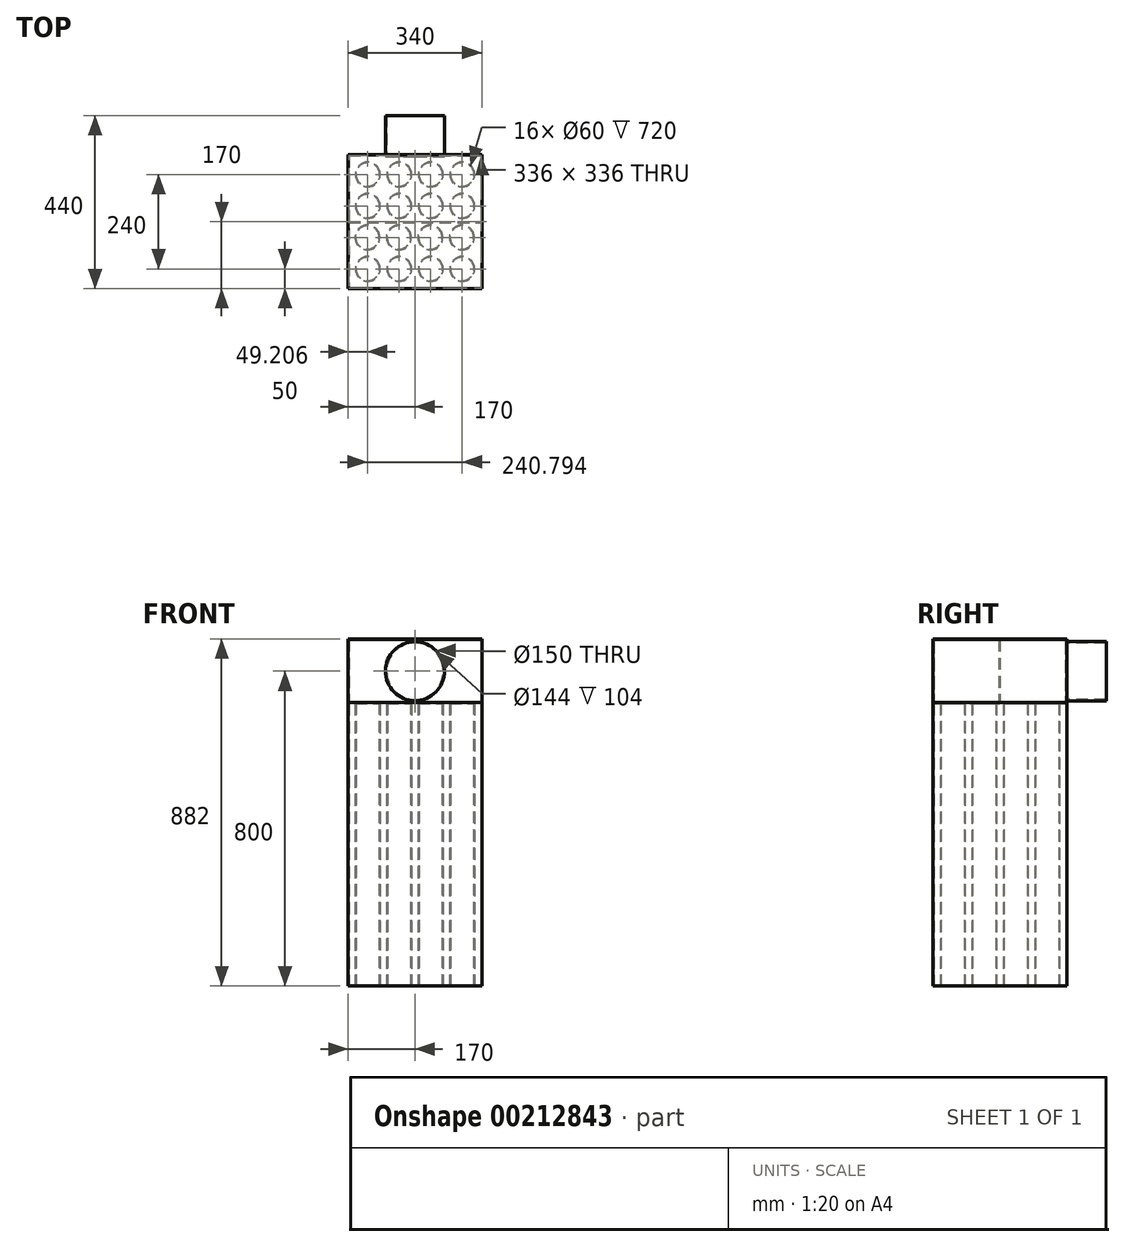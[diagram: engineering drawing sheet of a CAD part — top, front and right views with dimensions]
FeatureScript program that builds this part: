
annotation { "Feature Type Name" : "Feature", "Feature Type Description" : "" }
export const myFeature = defineFeature(function(context is Context, id is Id, definition is map)
    precondition{}
    {
        {
            var Q0;
            Q0=qCreatedBy(makeId("Top.planeOp"),FACE);
            var sketch = newSketch(context, id + "F0", { "sketchPlane" : qUnion([Q0])});
            skLineSegment(sketch, "E0.bottom", {"start": v(-170, 30.7) * mm, "end": v(170, 30.7) * mm});
            skLineSegment(sketch, "E0.top", {"start": v(-170, -309.3) * mm, "end": v(170, -309.3) * mm});
            skLineSegment(sketch, "E0.left", {"start": v(-170, 30.7) * mm, "end": v(-170, -309.3) * mm});
            skLineSegment(sketch, "E0.right", {"start": v(170, 30.7) * mm, "end": v(170, -309.3) * mm});
            skCircle(sketch, "E1", {"center": v(-120, -19.3) * mm, "radius": 30 * mm});
            skLineSegment(sketch, "E2.MirrorCS", {"start": v(-169.6, 306.05) * mm, "end": v(180.4, 306.05) * mm});
            skCircle(sketch, "E3", {"center": v(-40, -19.3) * mm, "radius": 30 * mm});
            skCircle(sketch, "E4", {"center": v(40, -19.3) * mm, "radius": 30 * mm});
            skCircle(sketch, "E5", {"center": v(120, -19.3) * mm, "radius": 30 * mm});
            skLineSegment(sketch, "E6", {"start": v(-170, 10.7) * mm, "end": v(170, 10.7) * mm, "construction": true});
            skLineSegment(sketch, "E7", {"start": v(150, 30.7) * mm, "end": v(150, -309.3) * mm, "construction": true});
            skCircle(sketch, "E8", {"center": v(120, -99.3) * mm, "radius": 30 * mm});
            skLineSegment(sketch, "E9", {"start": v(-170, -69.3) * mm, "end": v(170, -69.3) * mm, "construction": true});
            skLineSegment(sketch, "E10", {"start": v(-172.66, -149.3) * mm, "end": v(167.46, -149.3) * mm, "construction": true});
            skCircle(sketch, "E11", {"center": v(-120.8, -179.3) * mm, "radius": 30 * mm});
            skCircle(sketch, "E12", {"center": v(-40.8, -179.3) * mm, "radius": 30 * mm});
            skCircle(sketch, "E13", {"center": v(39.2, -179.3) * mm, "radius": 30 * mm});
            skCircle(sketch, "E14", {"center": v(119.2, -179.3) * mm, "radius": 30 * mm});
            skLineSegment(sketch, "E15", {"start": v(70, 30.7) * mm, "end": v(70, -309.3) * mm, "construction": true});
            skLineSegment(sketch, "E16", {"start": v(-10, 30.7) * mm, "end": v(-10, -309.3) * mm, "construction": true});
            skLineSegment(sketch, "E17", {"start": v(-90, 30.7) * mm, "end": v(-90, -309.3) * mm, "construction": true});
            skLineSegment(sketch, "E18", {"start": v(-170, -229.3) * mm, "end": v(170, -229.3) * mm, "construction": true});
            skCircle(sketch, "E19", {"center": v(-120, -99.3) * mm, "radius": 30 * mm});
            skCircle(sketch, "E20", {"center": v(-40, -99.3) * mm, "radius": 30 * mm});
            skCircle(sketch, "E21", {"center": v(40, -99.3) * mm, "radius": 30 * mm});
            skCircle(sketch, "E22", {"center": v(-120, -259.3) * mm, "radius": 30 * mm});
            skCircle(sketch, "E23", {"center": v(-40, -259.3) * mm, "radius": 30 * mm});
            skCircle(sketch, "E24", {"center": v(40, -259.3) * mm, "radius": 30 * mm});
            skCircle(sketch, "E25", {"center": v(120, -259.3) * mm, "radius": 30 * mm});
            skSolve(sketch);
        }
        {
            var Q0;
            Q0=makeQuery(id+"F0.imprint","IMPRINT",FACE,{"disambiguationData":[TD([[makeQuery(id+"F0.imprint","IMPRINT",EDGE,{"derivedFrom":sQuery(id+"F0.wireOp",EDGE,"E0.bottom")}),-1.0]])]});
            extrude(context, id + "F1", {"entities" : qUnion([Q0]), "endBound" : BoundingType.SYMMETRIC, "depth" : 720 * mm});
        }
        {
            var Q0;
            Q0=makeQuery(id+"F1.opExtrude","CAP_FACE",FACE,{"disambiguationData":[OSD([sQuery(id+"F0.wireOp",EDGE,"E0.bottom"),sQuery(id+"F0.wireOp",EDGE,"E0.top"),sQuery(id+"F0.wireOp",EDGE,"E0.left"),sQuery(id+"F0.wireOp",EDGE,"E0.right"),sQuery(id+"F0.wireOp",EDGE,"E1"),sQuery(id+"F0.wireOp",EDGE,"E3"),sQuery(id+"F0.wireOp",EDGE,"E4"),sQuery(id+"F0.wireOp",EDGE,"E5"),sQuery(id+"F0.wireOp",EDGE,"E8"),sQuery(id+"F0.wireOp",EDGE,"E11"),sQuery(id+"F0.wireOp",EDGE,"E12"),sQuery(id+"F0.wireOp",EDGE,"E13"),sQuery(id+"F0.wireOp",EDGE,"E14"),sQuery(id+"F0.wireOp",EDGE,"E19"),sQuery(id+"F0.wireOp",EDGE,"E20"),sQuery(id+"F0.wireOp",EDGE,"E21"),sQuery(id+"F0.wireOp",EDGE,"E22"),sQuery(id+"F0.wireOp",EDGE,"E23"),sQuery(id+"F0.wireOp",EDGE,"E24"),sQuery(id+"F0.wireOp",EDGE,"E25")])],"isStart":false});
            var sketch = newSketch(context, id + "F2", { "sketchPlane" : qUnion([Q0])});
            skLineSegment(sketch, "E26.0", {"start": v(-168, 28.7) * mm, "end": v(-168, -307.3) * mm});
            skLineSegment(sketch, "E26.1", {"start": v(-168, 28.7) * mm, "end": v(168, 28.7) * mm});
            skLineSegment(sketch, "E26.2", {"start": v(168, 28.7) * mm, "end": v(168, -307.3) * mm});
            skLineSegment(sketch, "E26.3", {"start": v(-168, -307.3) * mm, "end": v(168, -307.3) * mm});
            skSolve(sketch);
        }
        {
            var Q0;
            Q0=makeQuery(id+"F2.imprint","IMPRINT",FACE,{"disambiguationData":[TD([[makeQuery(id+"F2.imprint","IMPRINT",EDGE,{"derivedFrom":sQuery(id+"F2.wireOp",EDGE,"E26.0")}),-1.0]])]});
            extrude(context, id + "F3", {"entities" : qUnion([Q0]), "depth" : 160 * mm});
        }
        {
            var Q0;
            Q0=makeQuery(id+"F3.opExtrude","SWEPT_FACE",FACE,{"disambiguationData":[OSD([sQuery(id+"F2.wireOp",EDGE,"E26.2")])]});
            var sketch = newSketch(context, id + "F4", { "sketchPlane" : qUnion([Q0])});
            skLineSegment(sketch, "E27.bottom", {"start": v(139.3, 520) * mm, "end": v(141.3, 520) * mm});
            skLineSegment(sketch, "E27.top", {"start": v(139.3, 360) * mm, "end": v(141.3, 360) * mm});
            skLineSegment(sketch, "E27.left", {"start": v(139.3, 520) * mm, "end": v(139.3, 360) * mm});
            skLineSegment(sketch, "E27.right", {"start": v(141.3, 520) * mm, "end": v(141.3, 360) * mm});
            skLineSegment(sketch, "E28", {"start": v(140.3, 520) * mm, "end": v(140.3, 360) * mm, "construction": true});
            skSolve(sketch);
        }
        {
            var Q0;
            Q0=makeQuery(id+"F4.imprint","IMPRINT",FACE,{"disambiguationData":[TD([[makeQuery(id+"F4.imprint","IMPRINT",EDGE,{"derivedFrom":sQuery(id+"F4.wireOp",EDGE,"E27.bottom")}),-1.0]])]});
            extrude(context, id + "F5", {"entities" : qUnion([Q0]), "depth" : 336 * mm});
        }
        {
            var Q0;
            Q0=makeQuery(id+"F3.opExtrude","CAP_FACE",FACE,{"disambiguationData":[OSD([sQuery(id+"F0.wireOp",EDGE,"E0.bottom"),sQuery(id+"F0.wireOp",EDGE,"E0.top"),sQuery(id+"F0.wireOp",EDGE,"E0.left"),sQuery(id+"F0.wireOp",EDGE,"E0.right"),sQuery(id+"F2.wireOp",EDGE,"E26.0"),sQuery(id+"F2.wireOp",EDGE,"E26.1"),sQuery(id+"F2.wireOp",EDGE,"E26.2"),sQuery(id+"F2.wireOp",EDGE,"E26.3")])],"isStart":false});
            var sketch = newSketch(context, id + "F6", { "sketchPlane" : qUnion([Q0])});
            skLineSegment(sketch, "E29.bottom", {"start": v(-170, 30.7) * mm, "end": v(170, 30.7) * mm});
            skLineSegment(sketch, "E29.top", {"start": v(-170, -309.3) * mm, "end": v(170, -309.3) * mm});
            skLineSegment(sketch, "E29.left", {"start": v(-170, 30.7) * mm, "end": v(-170, -309.3) * mm});
            skLineSegment(sketch, "E29.right", {"start": v(170, 30.7) * mm, "end": v(170, -309.3) * mm});
            skSolve(sketch);
        }
        {
            var Q0;
            Q0 = qSketchRegion(id + "F6", true);
            extrude(context, id + "F7", {"entities" : qUnion([Q0]), "depth" : 2 * mm});
        }
        {
            var Q0;
            Q0=makeQuery(id+"F3.opExtrude","SWEPT_FACE",FACE,{"disambiguationData":[OSD([sQuery(id+"F0.wireOp",EDGE,"E0.top")])]});
            var sketch = newSketch(context, id + "F8", { "sketchPlane" : qUnion([Q0])});
            skCircle(sketch, "E30", {"center": v(0, 440) * mm, "radius": 75 * mm});
            skPoint(sketch, "E30.centerSnap0", {"position": v(170, 440) * mm});
            skSolve(sketch);
        }
        {
            var Q0;
            Q0 = qSketchRegion(id + "F8", true);
            extrude(context, id + "F9", {"entities" : qUnion([Q0]), "operationType" : NewBodyOperationType.REMOVE, "endBound" : BoundingType.SYMMETRIC, "depth" : 25 * mm});
        }
        {
            var Q0;
            Q0=makeQuery(id+"F3.opExtrude","SWEPT_FACE",FACE,{"disambiguationData":[OSD([sQuery(id+"F0.wireOp",EDGE,"E0.top")])]});
            var sketch = newSketch(context, id + "F10", { "sketchPlane" : qUnion([Q0])});
            skCircle(sketch, "E31", {"center": v(0, 440) * mm, "radius": 75 * mm});
            skCircle(sketch, "E32.0", {"center": v(0, 440) * mm, "radius": 72 * mm});
            skSolve(sketch);
        }
        {
            var Q0;
            Q0=sQuery(id+"F10.wireOp",EDGE,"E32.0");
            var Q1;
            Q1=sQuery(id+"F10.wireOp",EDGE,"E31");
            extrude(context, id + "F11", {"bodyType" : ToolBodyType.SURFACE, "surfaceEntities" : qUnion([Q0, Q1]), "depth" : 100 * mm, "hasSecondDirection" : true, "secondDirectionOppositeDirection" : true, "secondDirectionDepth" : 6 * mm});
        }
        {
            var Q0;
            Q0=makeQuery(id+"F3.opExtrude","SWEPT_FACE",FACE,{"disambiguationData":[OSD([sQuery(id+"F0.wireOp",EDGE,"E0.bottom")])]});
            var sketch = newSketch(context, id + "F12", { "sketchPlane" : qUnion([Q0])});
            skCircle(sketch, "E33", {"center": v(0, 440) * mm, "radius": 75 * mm});
            skPoint(sketch, "E33.centerSnap0", {"position": v(170, 440) * mm});
            skSolve(sketch);
        }
        {
            var Q0;
            Q0 = qSketchRegion(id + "F12", true);
            extrude(context, id + "F13", {"entities" : qUnion([Q0]), "operationType" : NewBodyOperationType.REMOVE, "oppositeDirection" : true, "depth" : 25 * mm});
        }
        {
            var Q0;
            Q0=makeQuery(id+"F3.opExtrude","SWEPT_FACE",FACE,{"disambiguationData":[OSD([sQuery(id+"F0.wireOp",EDGE,"E0.bottom")])]});
            var sketch = newSketch(context, id + "F14", { "sketchPlane" : qUnion([Q0])});
            skCircle(sketch, "E34", {"center": v(0, 440) * mm, "radius": 75 * mm});
            skCircle(sketch, "E35.0", {"center": v(0, 440) * mm, "radius": 72 * mm});
            skSolve(sketch);
        }
        {
            var Q0;
            Q0 = qSketchRegion(id + "F14", true);
            extrude(context, id + "F15", {"entities" : qUnion([Q0]), "operationType" : NewBodyOperationType.ADD, "depth" : 100 * mm, "hasSecondDirection" : true, "secondDirectionOppositeDirection" : true, "secondDirectionDepth" : 4 * mm});
        }
        {
            var Q0;
            Q0=makeQuery(id+"F1.opExtrude","CAP_FACE",FACE,{"disambiguationData":[OSD([sQuery(id+"F0.wireOp",EDGE,"E0.bottom"),sQuery(id+"F0.wireOp",EDGE,"E0.top"),sQuery(id+"F0.wireOp",EDGE,"E0.left"),sQuery(id+"F0.wireOp",EDGE,"E0.right"),sQuery(id+"F0.wireOp",EDGE,"E1"),sQuery(id+"F0.wireOp",EDGE,"E3"),sQuery(id+"F0.wireOp",EDGE,"E4"),sQuery(id+"F0.wireOp",EDGE,"E5"),sQuery(id+"F0.wireOp",EDGE,"E8"),sQuery(id+"F0.wireOp",EDGE,"E11"),sQuery(id+"F0.wireOp",EDGE,"E12"),sQuery(id+"F0.wireOp",EDGE,"E13"),sQuery(id+"F0.wireOp",EDGE,"E14"),sQuery(id+"F0.wireOp",EDGE,"E19"),sQuery(id+"F0.wireOp",EDGE,"E20"),sQuery(id+"F0.wireOp",EDGE,"E21"),sQuery(id+"F0.wireOp",EDGE,"E22"),sQuery(id+"F0.wireOp",EDGE,"E23"),sQuery(id+"F0.wireOp",EDGE,"E24"),sQuery(id+"F0.wireOp",EDGE,"E25")])],"isStart":true});
            var sketch = newSketch(context, id + "F16", { "sketchPlane" : qUnion([Q0])});
            skLineSegment(sketch, "E36.0", {"start": v(-168, 307.3) * mm, "end": v(-168, -28.7) * mm});
            skLineSegment(sketch, "E36.1", {"start": v(168, 307.3) * mm, "end": v(-168, 307.3) * mm});
            skLineSegment(sketch, "E36.2", {"start": v(168, -28.7) * mm, "end": v(168, 307.3) * mm});
            skLineSegment(sketch, "E36.3", {"start": v(-168, -28.7) * mm, "end": v(168, -28.7) * mm});
            skCircle(sketch, "E37.0", {"center": v(-120.8, 179.3) * mm, "radius": 31.5 * mm});
            skLineSegment(sketch, "E38.1", {"start": v(165, 304.3) * mm, "end": v(-165, 304.3) * mm});
            skLineSegment(sketch, "E38.2", {"start": v(165, -25.7) * mm, "end": v(165, 304.3) * mm});
            skLineSegment(sketch, "E38.3", {"start": v(-165, -25.7) * mm, "end": v(165, -25.7) * mm});
            skCircle(sketch, "E39.0", {"center": v(-120, 259.3) * mm, "radius": 31.5 * mm});
            skCircle(sketch, "E40.0", {"center": v(-40, 259.3) * mm, "radius": 31.5 * mm});
            skCircle(sketch, "E41.0", {"center": v(40, 259.3) * mm, "radius": 31.5 * mm});
            skCircle(sketch, "E42.0", {"center": v(120, 259.3) * mm, "radius": 31.5 * mm});
            skCircle(sketch, "E43.0", {"center": v(-40.8, 179.3) * mm, "radius": 31.5 * mm});
            skCircle(sketch, "E44.0", {"center": v(39.2, 179.3) * mm, "radius": 31.5 * mm});
            skCircle(sketch, "E45.0", {"center": v(119.2, 179.3) * mm, "radius": 31.5 * mm});
            skCircle(sketch, "E46.0", {"center": v(-120, 99.3) * mm, "radius": 31.5 * mm});
            skCircle(sketch, "E47.0", {"center": v(-40, 99.3) * mm, "radius": 31.5 * mm});
            skCircle(sketch, "E48.0", {"center": v(40, 99.3) * mm, "radius": 31.5 * mm});
            skCircle(sketch, "E49.0", {"center": v(-120, 19.3) * mm, "radius": 31.5 * mm});
            skCircle(sketch, "E50.0", {"center": v(-40, 19.3) * mm, "radius": 31.5 * mm});
            skCircle(sketch, "E51.0", {"center": v(120, 99.3) * mm, "radius": 31.5 * mm});
            skCircle(sketch, "E52.0", {"center": v(40, 19.3) * mm, "radius": 31.5 * mm});
            skCircle(sketch, "E53.0", {"center": v(120, 19.3) * mm, "radius": 31.5 * mm});
            skSolve(sketch);
        }
        {
            var Q0;
            Q0=makeQuery(id+"F16.imprint","IMPRINT",FACE,{"disambiguationData":[TD([[makeQuery(id+"F16.imprint","IMPRINT",EDGE,{"derivedFrom":sQuery(id+"F16.wireOp",EDGE,"E36.0")}),1.0]])]});
            extrude(context, id + "F17", {"entities" : qUnion([Q0]), "operationType" : NewBodyOperationType.REMOVE, "oppositeDirection" : true, "depth" : 718 * mm});
        }
    });
